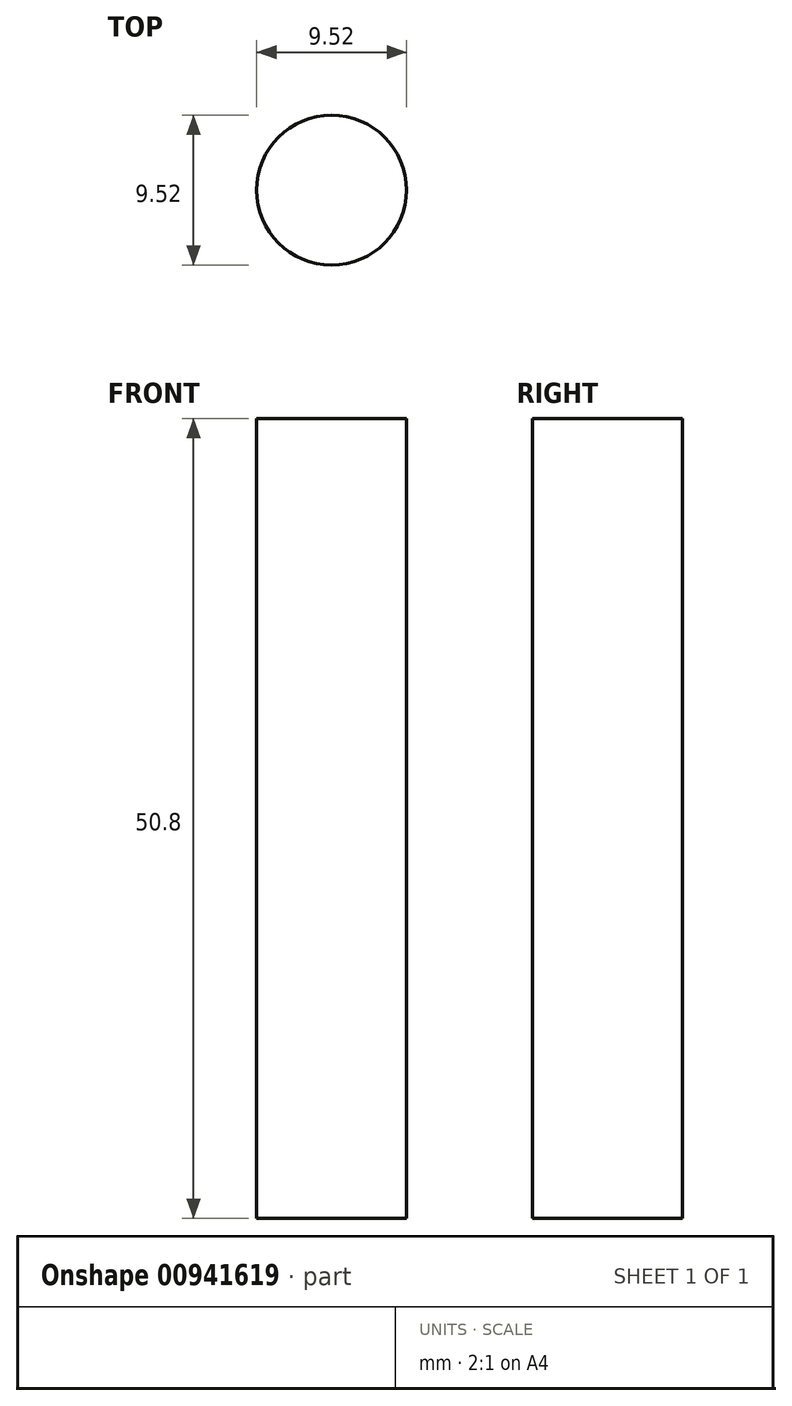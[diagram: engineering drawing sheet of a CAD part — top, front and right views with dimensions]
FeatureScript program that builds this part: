
annotation { "Feature Type Name" : "Feature", "Feature Type Description" : "" }
export const myFeature = defineFeature(function(context is Context, id is Id, definition is map)
    precondition{}
    {
        {
            var Q0;
            Q0=qCreatedBy(makeId("Top.planeOp"),FACE);
            var sketch = newSketch(context, id + "F0", { "sketchPlane" : qUnion([Q0])});
            skCircle(sketch, "E0", {"center": v(0, 0) * mm, "radius": 4.76 * mm});
            skSolve(sketch);
        }
        {
            var Q0;
            Q0=makeQuery(id+"F0.imprint","IMPRINT",FACE,{"disambiguationData":[TD([[makeQuery(id+"F0.imprint","IMPRINT",EDGE,{"derivedFrom":sQuery(id+"F0.wireOp",EDGE,"E0")}),1.0]])]});
            extrude(context, id + "F1", {"entities" : qUnion([Q0]), "endBound" : BoundingType.SYMMETRIC, "depth" : 50.8 * mm, "offsetDistance" : 25.4 * mm});
        }
    });
